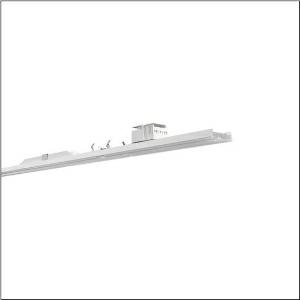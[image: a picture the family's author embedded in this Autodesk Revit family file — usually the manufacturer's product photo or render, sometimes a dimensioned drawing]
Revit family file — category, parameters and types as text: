
# Revit family: licross_r__11_recessed_ho_51tl12dn4dxl3s_8abb
name_source: partatom
category: Lighting Fixtures
units: mm (PartAtom-declared; Revit-internal decimal feet)

## family parameters
Cut with Voids When Loaded = No
Host = Face
Light Source = No
Part Type = Normal
Room Calculation Point = No
Round Connector Dimension = Use Diameter
Shared = No

## types (1)
- --- (1 x LED, 880 lm, 5 W, 4000K)
    Apparent Load = 5 VA
    CIE Flux Codes = 66 91 98 100 100
    Color Rendering = 80
    Color Temperature = 4000K
    Default Elevation = 1800 mm
    Description = Licross® 11 Recessed HO, luminaire insert, of sheet steel, galvanised, coil coated, white, length: 1.500mm, width: 66mm, height: 67mm, LED rated luminous flux: 13.000lm, light colour: 840, control gear: DALI 2, control gear: ECG DALI, with plug, 6-pole, with phase selection, for trunking rail, 14-core, mains connection: 220..240V, AC/DC, 0/50..60Hz, for emergency light function, halogen-free wiring, converter,control gear: single battery element, battery: LiFeP04, 9Ah, primary optical cover: cover, of PMMA, light emission: direct distribution, protection rating (complete): IP40, insulation class (complete): insulation class I (protective earthing), certification: CE, UKCA, protection symbol: D if used in an environment without relevant dust loads with corresponding accessories, permissible ambient temperature for indoor applications: +5..+30°C, standard: EN 60598-2-22, corresponds to IFS (International Featured Standards) requirements for safety and quality in the food industry, reducing of maximum allowable ambient temperature of 5°C with ceiling mounting, LABS conformity tested according to VDMA 24364:2018-05, packaging unit: 1 piece
    Height = 58 mm
    Lamp = 1 x LED
    Lamp Light Flux = 880 lm
    Lamp Power = 5 W
    Lamp count = 1
    Length = 1500 mm
    Luminous efficacy = 176 lm/W
    Manufacturer = Siteco
    ModVariant = No
    Model = 51TL12DN4DXL3S
    Mounting Place = Ceiling
    Mounting Type = Pendant
    Number of Poles = 1
    OnlyDefault = Yes
    Power Factor = 1
    Product Name = Licross® 11 Recessed HO
    Product group = luminaire insert
    ProductGroupID = 902
    Protection Class = Protection class I
    Protection Degree = IP 40
    RLX_Detail_Level = 1
    RlxData = <blob elided: 22937 chars, md5=2182e862>
    Socket = socket
    Standby Power = 0 W
    System Light Flux = 880 lm
    System Power = 5 W
    Type Comments = : emergency light operation: 3 h
    Type Image = l_1266722.jpg
    URL = http://relux.com
    VarID = @adj_125815
    Voltage = 0 V
    Weight = 0.00 kg
    Width = 66 mm

## geometry (parser evidence)
native form markers: Blend x4, Sweep x11
no freeform markers — native parametric forms only
